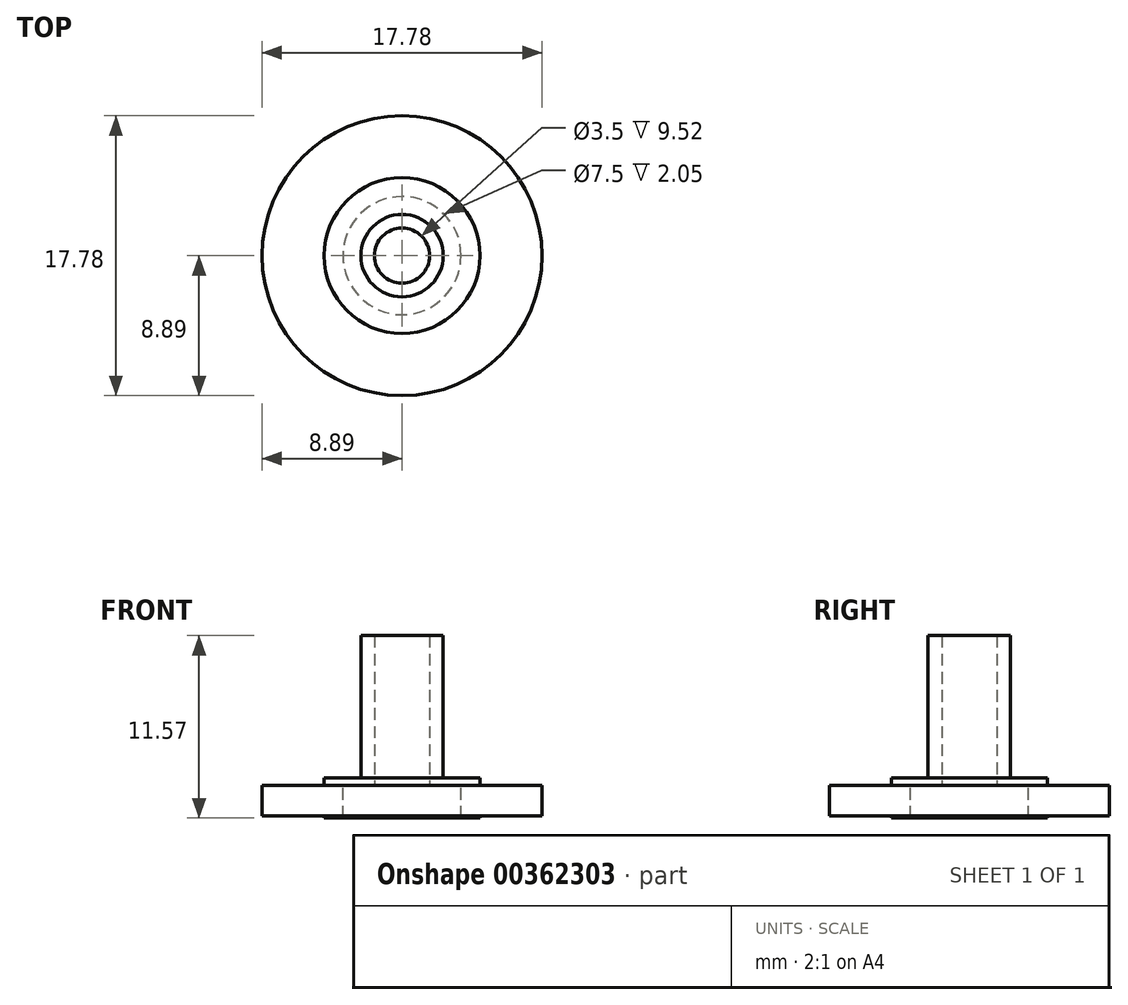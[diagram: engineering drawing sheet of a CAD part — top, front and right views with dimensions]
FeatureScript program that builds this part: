
annotation { "Feature Type Name" : "Feature", "Feature Type Description" : "" }
export const myFeature = defineFeature(function(context is Context, id is Id, definition is map)
    precondition{}
    {
        {
            var Q0;
            Q0=qCreatedBy(makeId("Top.planeOp"),FACE);
            var sketch = newSketch(context, id + "F0", { "sketchPlane" : qUnion([Q0])});
            skCircle(sketch, "E0", {"center": v(0, 0) * mm, "radius": 1.75 * mm});
            skCircle(sketch, "E1", {"center": v(0, 0) * mm, "radius": 2.62 * mm});
            skCircle(sketch, "E2", {"center": v(0, 0) * mm, "radius": 3.75 * mm});
            skCircle(sketch, "E3", {"center": v(0, 0) * mm, "radius": 8.9 * mm});
            skCircle(sketch, "E4", {"center": v(0, 0) * mm, "radius": 4.95 * mm});
            skSolve(sketch);
        }
        {
            var Q0;
            Q0=makeQuery(id+"F0.imprint","IMPRINT",FACE,{"disambiguationData":[TD([[makeQuery(id+"F0.imprint","IMPRINT",EDGE,{"derivedFrom":sQuery(id+"F0.wireOp",EDGE,"E0")}),-1.0]])]});
            extrude(context, id + "F1", {"entities" : qUnion([Q0]), "depth" : 9.52 * mm});
        }
        {
            var Q0;
            Q0=makeQuery(id+"F0.imprint","IMPRINT",FACE,{"disambiguationData":[TD([[makeQuery(id+"F0.imprint","IMPRINT",EDGE,{"derivedFrom":sQuery(id+"F0.wireOp",EDGE,"E2")}),-1.0]])]});
            var Q1;
            Q1=makeQuery(id+"F0.imprint","IMPRINT",FACE,{"disambiguationData":[TD([[makeQuery(id+"F0.imprint","IMPRINT",EDGE,{"derivedFrom":sQuery(id+"F0.wireOp",EDGE,"E1")}),-1.0]])]});
            extrude(context, id + "F2", {"entities" : qUnion([Q0, Q1]), "operationType" : NewBodyOperationType.ADD, "depth" : 0.48 * mm});
        }
        {
            var Q0;
            Q0=makeQuery(id+"F0.imprint","IMPRINT",FACE,{"disambiguationData":[TD([[makeQuery(id+"F0.imprint","IMPRINT",EDGE,{"derivedFrom":sQuery(id+"F0.wireOp",EDGE,"E2")}),-1.0]])]});
            extrude(context, id + "F3", {"entities" : qUnion([Q0]), "operationType" : NewBodyOperationType.ADD, "oppositeDirection" : true, "depth" : 2.05 * mm});
        }
        {
            var Q0;
            Q0=makeQuery(id+"F0.imprint","IMPRINT",FACE,{"disambiguationData":[TD([[makeQuery(id+"F0.imprint","IMPRINT",EDGE,{"derivedFrom":sQuery(id+"F0.wireOp",EDGE,"E3")}),1.0]])]});
            extrude(context, id + "F4", {"entities" : qUnion([Q0]), "operationType" : NewBodyOperationType.ADD, "oppositeDirection" : true, "depth" : 1.92 * mm});
        }
    });
